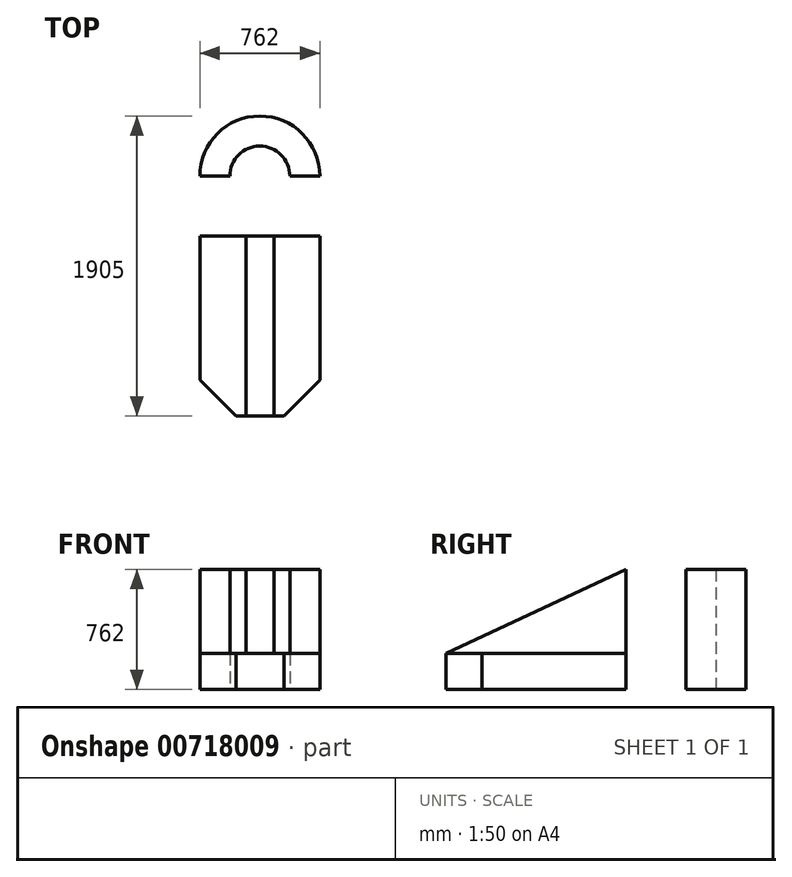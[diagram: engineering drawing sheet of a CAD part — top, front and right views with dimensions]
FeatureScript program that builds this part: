
annotation { "Feature Type Name" : "Feature", "Feature Type Description" : "" }
export const myFeature = defineFeature(function(context is Context, id is Id, definition is map)
    precondition{}
    {
        {
            var Q0;
            Q0=qCreatedBy(makeId("Top.planeOp"),FACE);
            var sketch = newSketch(context, id + "F0", { "sketchPlane" : qUnion([Q0])});
            skLineSegment(sketch, "E0.bottom", {"start": v(-363.59, 883.7) * mm, "end": v(398.41, 883.7) * mm});
            skLineSegment(sketch, "E0.top", {"start": v(-134.99, -640.3) * mm, "end": v(169.81, -640.3) * mm});
            skLineSegment(sketch, "E0.left", {"start": v(-363.59, 883.7) * mm, "end": v(-363.59, -411.7) * mm});
            skLineSegment(sketch, "E0.right", {"start": v(398.41, 883.7) * mm, "end": v(398.41, -411.7) * mm});
            skLineSegment(sketch, "E1", {"start": v(-363.59, -411.7) * mm, "end": v(-134.99, -640.3) * mm});
            skLineSegment(sketch, "E2", {"start": v(169.81, -640.3) * mm, "end": v(398.41, -411.7) * mm});
            skArc(sketch, "E3", {"start": v(398.41, 883.7) * mm, "mid": v(17.41, 1264.7) * mm, "end": v(-363.59, 883.7) * mm});
            skCircle(sketch, "E4", {"center": v(17.41, 883.7) * mm, "radius": 190.5 * mm});
            skLineSegment(sketch, "E5", {"start": v(-363.59, 502.7) * mm, "end": v(398.41, 502.7) * mm});
            skLineSegment(sketch, "E6.bottom", {"start": v(-71.49, -640.3) * mm, "end": v(106.31, -640.3) * mm});
            skLineSegment(sketch, "E6.top", {"start": v(-71.49, 502.7) * mm, "end": v(106.31, 502.7) * mm});
            skLineSegment(sketch, "E6.left", {"start": v(-71.49, -640.3) * mm, "end": v(-71.49, 502.7) * mm});
            skLineSegment(sketch, "E6.right", {"start": v(106.31, -640.3) * mm, "end": v(106.31, 502.7) * mm});
            skSolve(sketch);
        }
        {
            var Q0;
            {var subQ0=sQuery(id+"F0.wireOp",EDGE,"E4");var subQ1=sQuery(id+"F0.wireOp",EDGE,"E0.bottom");var subQ2=makeQuery(id+"F0.imprint","INTERSECT",VERTEX,{"disambiguationData":[OD(0.0)],"derivedFrom":[subQ1,subQ0]});var subQ3=sQuery(id+"F0.wireOp",EDGE,"E3");var subQ11=sQuery(id+"F0.wireOp",EDGE,"E6.left");var subQ16=makeQuery(id+"F0.imprint","IMPRINT",EDGE,{"derivedFrom":subQ11});var subQ24=sQuery(id+"F0.wireOp",EDGE,"E1");var subQ27=sQuery(id+"F0.wireOp",EDGE,"E2");Q0=qUnion([makeQuery(id+"F0.imprint","IMPRINT",FACE,{"disambiguationData":[TD([[makeQuery(id+"F0.imprint","IMPRINT",EDGE,{"derivedFrom":subQ27}),1.0]])]}),makeQuery(id+"F0.imprint","IMPRINT",FACE,{"disambiguationData":[TD([[makeQuery(id+"F0.imprint","IMPRINT",EDGE,{"disambiguationData":[TD([[subQ2,-1.0]])],"derivedFrom":subQ0}),-1.0]])]}),makeQuery(id+"F0.imprint","IMPRINT",FACE,{"disambiguationData":[TD([[makeQuery(id+"F0.imprint","IMPRINT",EDGE,{"derivedFrom":subQ24}),1.0]])]}),makeQuery(id+"F0.imprint","IMPRINT",FACE,{"disambiguationData":[TD([[subQ16,-1.0]])]}),makeQuery(id+"F0.imprint","IMPRINT",FACE,{"disambiguationData":[TD([[makeQuery(id+"F0.imprint","IMPRINT",EDGE,{"derivedFrom":subQ3}),1.0]])]})]);}
            extrude(context, id + "F1", {"entities" : qUnion([Q0]), "depth" : 228.6 * mm, "offsetDistance" : 25.4 * mm});
        }
        {
            var Q0;
            {var subQ2=sQuery(id+"F0.wireOp",EDGE,"E0.bottom");var subQ9=sQuery(id+"F0.wireOp",EDGE,"E4");var subQ11=makeQuery(id+"F0.imprint","INTERSECT",VERTEX,{"disambiguationData":[OD(0.0)],"derivedFrom":[subQ2,subQ9]});Q0=makeQuery(id+"F0.imprint","IMPRINT",FACE,{"disambiguationData":[TD([[makeQuery(id+"F0.imprint","IMPRINT",EDGE,{"disambiguationData":[TD([[subQ11,-1.0]])],"derivedFrom":subQ9}),-1.0]])]});}
            var Q1;
            {var subQ0=sQuery(id+"F0.wireOp",EDGE,"E6.left");Q1=makeQuery(id+"F0.imprint","IMPRINT",FACE,{"disambiguationData":[TD([[makeQuery(id+"F0.imprint","IMPRINT",EDGE,{"derivedFrom":subQ0}),-1.0]])]});}
            var Q2;
            {var subQ3=sQuery(id+"F0.wireOp",EDGE,"E3");Q2=makeQuery(id+"F0.imprint","IMPRINT",FACE,{"disambiguationData":[TD([[makeQuery(id+"F0.imprint","IMPRINT",EDGE,{"derivedFrom":subQ3}),1.0]])]});}
            extrude(context, id + "F2", {"entities" : qUnion([Q0, Q1, Q2]), "operationType" : NewBodyOperationType.ADD, "depth" : 762 * mm, "offsetDistance" : 25.4 * mm});
        }
        {
            var Q0;
            Q0=makeQuery(id+"F2.opExtrude","SWEPT_FACE",FACE,{"disambiguationData":[OSD([sQuery(id+"F0.wireOp",EDGE,"E6.right")])]});
            var sketch = newSketch(context, id + "F3", { "sketchPlane" : qUnion([Q0])});
            skLineSegment(sketch, "E7", {"start": v(-640.3, 228.6) * mm, "end": v(502.7, 762) * mm});
            skSolve(sketch);
        }
        {
            var Q0;
            Q0=makeQuery(id+"F3.imprint","IMPRINT",FACE,{"disambiguationData":[TD([[makeQuery(id+"F3.imprint","IMPRINT",EDGE,{"derivedFrom":sQuery(id+"F3.wireOp",EDGE,"E7")}),1.0]])]});
            extrude(context, id + "F4", {"entities" : qUnion([Q0]), "operationType" : NewBodyOperationType.REMOVE, "oppositeDirection" : true, "depth" : 177.8 * mm, "offsetDistance" : 25.4 * mm});
        }
    });
